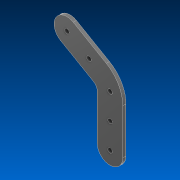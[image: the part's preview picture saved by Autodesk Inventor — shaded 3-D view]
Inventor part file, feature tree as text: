
AUTODESK INVENTOR PART (.ipt)
format: ipt  version: 2022.2 (Build 262287000, 287)  size: 112,640 bytes
history: native  units: in
note: dims shown in document units (in); Inventor stores cm internally (conversion verified against a paired STEP export)
features: sketch x1, extrude x1, hole x1
ambient origin geometry x8: Origin, YZ Plane, XZ Plane, XY Plane, X Axis, Y Axis, Z Axis, Center Point
bodies: Solid1 (feature_tree)
feature tree (3):
  sketch  "Sketch1"  dims[d0=1.0in d1=2.0in d2=1.0in d3=0.5in d4=0.125in d5=0.0in d6=60.0deg d7=0.175in d8=0.75in d9=0.375in d10=0.25in d11=0.5635in d12=1.0in d13=0.8108in d14=1.0in]
  extrude  "Extrusion1"  Depth=1.0in
  hole  "Hole1"  [1 undecoded]
note: 1 required parameter value undecoded (feature->parameter linkage not recoverable at this tier; creation-order binding heuristic only, values carry confidence <= 0.55)
